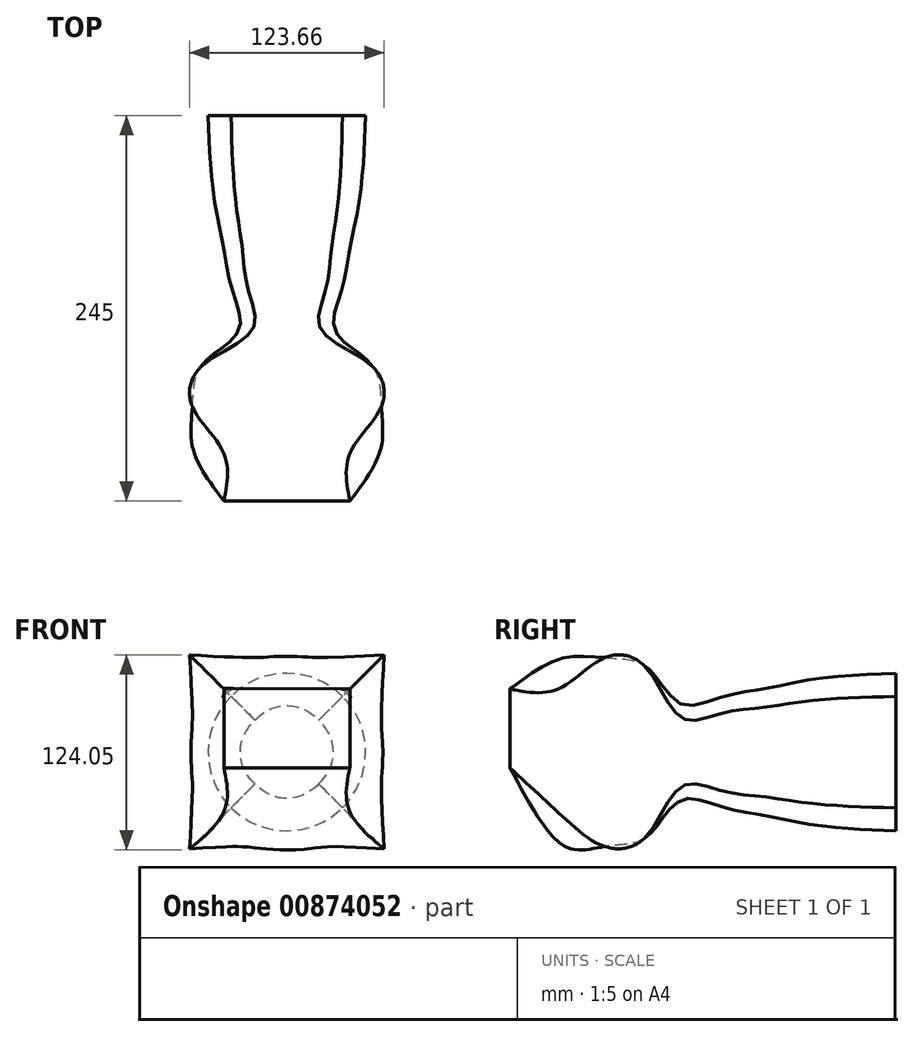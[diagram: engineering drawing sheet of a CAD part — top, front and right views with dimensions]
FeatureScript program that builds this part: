
annotation { "Feature Type Name" : "Feature", "Feature Type Description" : "" }
export const myFeature = defineFeature(function(context is Context, id is Id, definition is map)
    precondition{}
    {
        {
            var Q0;
            Q0=qCreatedBy(makeId("Front.planeOp"),FACE);
            cPlane(context, id + "F0", {"entities" : qUnion([Q0]), "cplaneType" : CPlaneType.OFFSET, "offset" : 60 * mm, "width" : 150 * mm, "height" : 150 * mm});
        }
        {
            var Q0;
            Q0=qCreatedBy(id+"F0.planeOp",FACE);
            var sketch = newSketch(context, id + "F1", { "sketchPlane" : qUnion([Q0])});
            skCircle(sketch, "E0", {"center": v(0, 0) * mm, "radius": 45 * mm});
            skSolve(sketch);
        }
        {
            var Q0;
            Q0=qCreatedBy(makeId("Front.planeOp"),FACE);
            var sketch = newSketch(context, id + "F2", { "sketchPlane" : qUnion([Q0])});
            skCircle(sketch, "E1", {"center": v(0, 0) * mm, "radius": 50 * mm});
            skSolve(sketch);
        }
        {
            var Q0;
            Q0=qCreatedBy(id+"F0.planeOp",FACE);
            cPlane(context, id + "F3", {"entities" : qUnion([Q0]), "cplaneType" : CPlaneType.OFFSET, "offset" : 25 * mm, "width" : 150 * mm, "height" : 150 * mm});
        }
        {
            var Q0;
            Q0=qCreatedBy(id+"F3.planeOp",FACE);
            var sketch = newSketch(context, id + "F4", { "sketchPlane" : qUnion([Q0])});
            skCircle(sketch, "E2", {"center": v(0, 0) * mm, "radius": 40 * mm});
            skSolve(sketch);
        }
        {
            var Q0;
            Q0=qCreatedBy(id+"F3.planeOp",FACE);
            cPlane(context, id + "F5", {"entities" : qUnion([Q0]), "cplaneType" : CPlaneType.OFFSET, "offset" : 25 * mm, "width" : 150 * mm, "height" : 150 * mm});
        }
        {
            var Q0;
            Q0=qCreatedBy(id+"F5.planeOp",FACE);
            var sketch = newSketch(context, id + "F6", { "sketchPlane" : qUnion([Q0])});
            skCircle(sketch, "E3", {"center": v(0, 0) * mm, "radius": 35 * mm});
            skSolve(sketch);
        }
        {
            var Q0;
            Q0=qCreatedBy(id+"F5.planeOp",FACE);
            cPlane(context, id + "F7", {"entities" : qUnion([Q0]), "cplaneType" : CPlaneType.OFFSET, "offset" : 25 * mm, "width" : 150 * mm, "height" : 150 * mm});
        }
        {
            var Q0;
            Q0=qCreatedBy(id+"F7.planeOp",FACE);
            var sketch = newSketch(context, id + "F8", { "sketchPlane" : qUnion([Q0])});
            skCircle(sketch, "E4", {"center": v(0, 0) * mm, "radius": 30 * mm});
            skSolve(sketch);
        }
        {
            var Q0;
            Q0=qCreatedBy(id+"F7.planeOp",FACE);
            cPlane(context, id + "F9", {"entities" : qUnion([Q0]), "cplaneType" : CPlaneType.OFFSET, "offset" : 25 * mm, "width" : 150 * mm, "height" : 150 * mm});
        }
        {
            var Q0;
            Q0=qCreatedBy(id+"F9.planeOp",FACE);
            var sketch = newSketch(context, id + "F10", { "sketchPlane" : qUnion([Q0])});
            skLineSegment(sketch, "E5.bottom", {"start": v(55, 55) * mm, "end": v(-55, 55) * mm});
            skLineSegment(sketch, "E5.top", {"start": v(55, -55) * mm, "end": v(-55, -55) * mm});
            skLineSegment(sketch, "E5.left", {"start": v(55, 55) * mm, "end": v(55, -55) * mm});
            skLineSegment(sketch, "E5.right", {"start": v(-55, 55) * mm, "end": v(-55, -55) * mm});
            skPoint(sketch, "E5.middle", {"position": v(0, 0) * mm});
            skSolve(sketch);
        }
        {
            var Q0;
            Q0=qCreatedBy(id+"F9.planeOp",FACE);
            cPlane(context, id + "F11", {"entities" : qUnion([Q0]), "cplaneType" : CPlaneType.OFFSET, "offset" : 25 * mm, "width" : 150 * mm, "height" : 150 * mm});
        }
        {
            var Q0;
            Q0=qCreatedBy(id+"F11.planeOp",FACE);
            var sketch = newSketch(context, id + "F12", { "sketchPlane" : qUnion([Q0])});
            skLineSegment(sketch, "E6.bottom", {"start": v(-60, 60) * mm, "end": v(60, 60) * mm});
            skLineSegment(sketch, "E6.top", {"start": v(-60, -60) * mm, "end": v(60, -60) * mm});
            skLineSegment(sketch, "E6.left", {"start": v(-60, 60) * mm, "end": v(-60, -60) * mm});
            skLineSegment(sketch, "E6.right", {"start": v(60, 60) * mm, "end": v(60, -60) * mm});
            skPoint(sketch, "E6.middle", {"position": v(0, 0) * mm});
            skSolve(sketch);
        }
        {
            var Q0;
            Q0=qCreatedBy(id+"F11.planeOp",FACE);
            cPlane(context, id + "F13", {"entities" : qUnion([Q0]), "cplaneType" : CPlaneType.OFFSET, "offset" : 25 * mm, "width" : 150 * mm, "height" : 150 * mm});
        }
        {
            var Q0;
            Q0=qCreatedBy(id+"F13.planeOp",FACE);
            var sketch = newSketch(context, id + "F14", { "sketchPlane" : qUnion([Q0])});
            skCircle(sketch, "E7", {"center": v(0, 0) * mm, "radius": 60 * mm});
            skSolve(sketch);
        }
        {
            var Q0;
            Q0=qCreatedBy(id+"F13.planeOp",FACE);
            cPlane(context, id + "F15", {"entities" : qUnion([Q0]), "cplaneType" : CPlaneType.OFFSET, "offset" : 35 * mm, "width" : 150 * mm, "height" : 150 * mm});
        }
        {
            var Q0;
            Q0=qCreatedBy(id+"F15.planeOp",FACE);
            var sketch = newSketch(context, id + "F16", { "sketchPlane" : qUnion([Q0])});
            skLineSegment(sketch, "E8.right", {"start": v(40, 40) * mm, "end": v(40, 40) * mm});
            skLineSegment(sketch, "E9.top", {"start": v(-40, -10) * mm, "end": v(40, -10) * mm});
            skLineSegment(sketch, "E9.left", {"start": v(-40, 40.54) * mm, "end": v(-40, -10) * mm});
            skLineSegment(sketch, "E10", {"start": v(40, 40) * mm, "end": v(40, -10) * mm});
            skLineSegment(sketch, "E11", {"start": v(-40, 40.54) * mm, "end": v(40, 40) * mm});
            skSolve(sketch);
        }
        {
            var Q0;
            Q0=makeQuery(id+"F2.imprint","IMPRINT",FACE,{"disambiguationData":[TD([[makeQuery(id+"F2.imprint","IMPRINT",EDGE,{"derivedFrom":sQuery(id+"F2.wireOp",EDGE,"E1")}),1.0]])]});
            var Q1;
            Q1=makeQuery(id+"F1.imprint","IMPRINT",FACE,{"disambiguationData":[TD([[makeQuery(id+"F1.imprint","IMPRINT",EDGE,{"derivedFrom":sQuery(id+"F1.wireOp",EDGE,"E0")}),1.0]])]});
            var Q2;
            Q2=makeQuery(id+"F4.imprint","IMPRINT",FACE,{"disambiguationData":[TD([[makeQuery(id+"F4.imprint","IMPRINT",EDGE,{"derivedFrom":sQuery(id+"F4.wireOp",EDGE,"E2")}),1.0]])]});
            var Q3;
            Q3=makeQuery(id+"F6.imprint","IMPRINT",FACE,{"disambiguationData":[TD([[makeQuery(id+"F6.imprint","IMPRINT",EDGE,{"derivedFrom":sQuery(id+"F6.wireOp",EDGE,"E3")}),1.0]])]});
            var Q4;
            Q4=makeQuery(id+"F8.imprint","IMPRINT",FACE,{"disambiguationData":[TD([[makeQuery(id+"F8.imprint","IMPRINT",EDGE,{"derivedFrom":sQuery(id+"F8.wireOp",EDGE,"E4")}),1.0]])]});
            var Q5;
            Q5=makeQuery(id+"F10.imprint","IMPRINT",FACE,{"disambiguationData":[TD([[makeQuery(id+"F10.imprint","IMPRINT",EDGE,{"derivedFrom":sQuery(id+"F10.wireOp",EDGE,"E5.bottom")}),1.0]])]});
            var Q6;
            Q6=makeQuery(id+"F12.imprint","IMPRINT",FACE,{"disambiguationData":[TD([[makeQuery(id+"F12.imprint","IMPRINT",EDGE,{"derivedFrom":sQuery(id+"F12.wireOp",EDGE,"E6.bottom")}),-1.0]])]});
            var Q7;
            Q7=makeQuery(id+"F14.imprint","IMPRINT",FACE,{"disambiguationData":[TD([[makeQuery(id+"F14.imprint","IMPRINT",EDGE,{"derivedFrom":sQuery(id+"F14.wireOp",EDGE,"E7")}),1.0]])]});
            var Q8;
            {var subQ0=sQuery(id+"F16.wireOp",EDGE,"E9.top");Q8=makeQuery(id+"F16.imprint","IMPRINT",FACE,{"disambiguationData":[TD([[makeQuery(id+"F16.imprint","IMPRINT",EDGE,{"derivedFrom":subQ0}),1.0]])]});}
            loft(context, id + "F17", {"sheetProfilesArray" : [{ "sheetProfileEntities" : qUnion([Q0]) }, { "sheetProfileEntities" : qUnion([Q1]) }, { "sheetProfileEntities" : qUnion([Q2]) }, { "sheetProfileEntities" : qUnion([Q3]) }, { "sheetProfileEntities" : qUnion([Q4]) }, { "sheetProfileEntities" : qUnion([Q5]) }, { "sheetProfileEntities" : qUnion([Q6]) }, { "sheetProfileEntities" : qUnion([Q7]) }, { "sheetProfileEntities" : qUnion([Q8]) }]});
        }
        {
            var Q0;
            Q0=qCreatedBy(id+"F15.planeOp",FACE);
            cPlane(context, id + "F18", {"entities" : qUnion([Q0]), "cplaneType" : CPlaneType.OFFSET, "offset" : 25 * mm, "width" : 150 * mm, "height" : 150 * mm});
        }
    });
